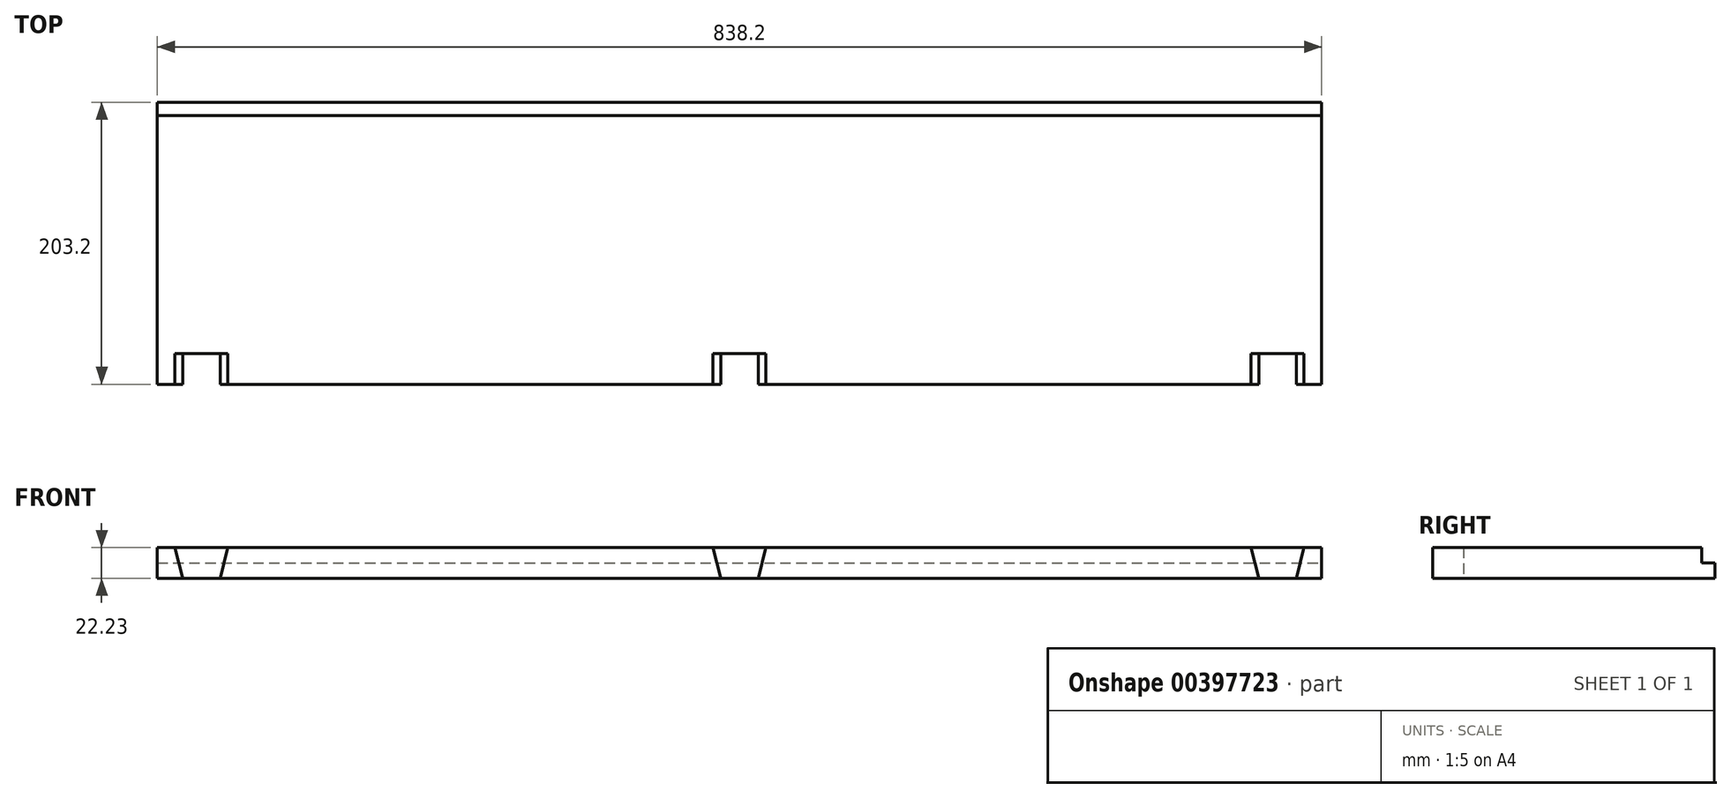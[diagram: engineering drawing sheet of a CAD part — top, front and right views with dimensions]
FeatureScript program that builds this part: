
annotation { "Feature Type Name" : "Feature", "Feature Type Description" : "" }
export const myFeature = defineFeature(function(context is Context, id is Id, definition is map)
    precondition{}
    {
        {
            var Q0;
            Q0=qCreatedBy(makeId("Top.planeOp"),FACE);
            var sketch = newSketch(context, id + "F0", { "sketchPlane" : qUnion([Q0])});
            skLineSegment(sketch, "E0.top", {"start": v(0, 0) * mm, "end": v(838.2, 0) * mm});
            skLineSegment(sketch, "E0.left", {"start": v(0, -203.2) * mm, "end": v(0, 0) * mm});
            skLineSegment(sketch, "E0.right", {"start": v(838.2, -203.2) * mm, "end": v(838.2, 0) * mm});
            skLineSegment(sketch, "E1.top", {"start": v(0, -203.2) * mm, "end": v(838.2, -203.2) * mm});
            skSolve(sketch);
        }
        {
            var Q0;
            Q0=makeQuery(id+"F0.imprint","IMPRINT",FACE,{"disambiguationData":[TD([[makeQuery(id+"F0.imprint","IMPRINT",EDGE,{"derivedFrom":sQuery(id+"F0.wireOp",EDGE,"E0.top")}),-1.0]])]});
            extrude(context, id + "F1", {"entities" : qUnion([Q0]), "depth" : 22.22 * mm});
        }
        {
            var Q0;
            Q0=makeQuery(id+"F1.opExtrude","CAP_FACE",FACE,{"disambiguationData":[OSD([sQuery(id+"F0.wireOp",EDGE,"E0.bottom"),sQuery(id+"F0.wireOp",EDGE,"E0.top"),sQuery(id+"F0.wireOp",EDGE,"E0.left"),sQuery(id+"F0.wireOp",EDGE,"E0.right"),sQuery(id+"F0.wireOp",EDGE,"E1.top"),sQuery(id+"F0.wireOp",EDGE,"E1.right"),sQuery(id+"F0.wireOp",EDGE,"6zvS0ofu-clFI-9DLG-dOLF-ekRLqX3uSt4N.top"),sQuery(id+"F0.wireOp",EDGE,"6zvS0ofu-clFI-9DLG-dOLF-ekRLqX3uSt4N.left")])],"isStart":false});
            var sketch = newSketch(context, id + "F2", { "sketchPlane" : qUnion([Q0])});
            skLineSegment(sketch, "E2.bottom", {"start": v(0, 0) * mm, "end": v(838.2, 0) * mm});
            skLineSegment(sketch, "E2.top", {"start": v(0, -9.52) * mm, "end": v(838.2, -9.52) * mm});
            skLineSegment(sketch, "E2.left", {"start": v(0, 0) * mm, "end": v(0, -9.52) * mm});
            skLineSegment(sketch, "E2.right", {"start": v(838.2, 0) * mm, "end": v(838.2, -9.52) * mm});
            skSolve(sketch);
        }
        {
            var Q0;
            Q0=makeQuery(id+"F2.imprint","IMPRINT",FACE,{"disambiguationData":[TD([[makeQuery(id+"F2.imprint","IMPRINT",EDGE,{"derivedFrom":sQuery(id+"F2.wireOp",EDGE,"E2.bottom")}),-1.0]])]});
            extrude(context, id + "F3", {"entities" : qUnion([Q0]), "operationType" : NewBodyOperationType.REMOVE, "oppositeDirection" : true, "depth" : 11.1 * mm});
        }
        {
            var Q0;
            Q0=makeQuery(id+"F1.opExtrude","SWEPT_FACE",FACE,{"disambiguationData":[OSD([sQuery(id+"F0.wireOp",EDGE,"E1.top")])]});
            var sketch = newSketch(context, id + "F4", { "sketchPlane" : qUnion([Q0])});
            skLineSegment(sketch, "E3", {"start": v(400.05, 22.23) * mm, "end": v(405.6, 0) * mm});
            skLineSegment(sketch, "E4", {"start": v(405.6, 0) * mm, "end": v(432.6, 0) * mm});
            skLineSegment(sketch, "E5", {"start": v(432.6, 0) * mm, "end": v(438.15, 22.23) * mm});
            skLineSegment(sketch, "E6", {"start": v(438.15, 22.23) * mm, "end": v(400.05, 22.23) * mm});
            skLineSegment(sketch, "E7.left", {"start": v(400.05, 22.23) * mm, "end": v(400.05, 0) * mm, "construction": true});
            skLineSegment(sketch, "E7.right", {"start": v(438.15, 22.23) * mm, "end": v(438.15, 0) * mm, "construction": true});
            skPoint(sketch, "E8", {"position": v(419.1, 22.23) * mm});
            skLineSegment(sketch, "E9", {"start": v(12.7, 22.23) * mm, "end": v(12.7, 0) * mm, "construction": true});
            skLineSegment(sketch, "E10", {"start": v(18.24, 0) * mm, "end": v(45.26, 0) * mm});
            skLineSegment(sketch, "E11", {"start": v(12.7, 22.23) * mm, "end": v(18.24, 0) * mm});
            skLineSegment(sketch, "E12", {"start": v(45.26, 0) * mm, "end": v(50.8, 22.23) * mm});
            skLineSegment(sketch, "E13", {"start": v(12.7, 0) * mm, "end": v(18.24, 0) * mm, "construction": true});
            skLineSegment(sketch, "E14.trimOffspring", {"start": v(50.8, 22.23) * mm, "end": v(12.7, 22.23) * mm});
            skLineSegment(sketch, "E15", {"start": v(825.5, 22.22) * mm, "end": v(787.4, 22.23) * mm});
            skLineSegment(sketch, "E16", {"start": v(787.4, 22.23) * mm, "end": v(787.4, 0) * mm, "construction": true});
            skLineSegment(sketch, "E17", {"start": v(787.4, 0) * mm, "end": v(792.94, 0) * mm, "construction": true});
            skLineSegment(sketch, "E18", {"start": v(792.94, 0) * mm, "end": v(787.4, 22.23) * mm});
            skLineSegment(sketch, "E19", {"start": v(825.5, 22.23) * mm, "end": v(825.5, 0) * mm, "construction": true});
            skLineSegment(sketch, "E20", {"start": v(825.5, 0) * mm, "end": v(819.96, 0) * mm, "construction": true});
            skLineSegment(sketch, "E21", {"start": v(825.5, 22.23) * mm, "end": v(819.96, 0) * mm});
            skLineSegment(sketch, "E22", {"start": v(792.94, 0) * mm, "end": v(819.96, 0) * mm});
            skSolve(sketch);
        }
        {
            var Q0;
            Q0=makeQuery(id+"F4.imprint","IMPRINT",FACE,{"disambiguationData":[TD([[makeQuery(id+"F4.imprint","IMPRINT",EDGE,{"derivedFrom":sQuery(id+"F4.wireOp",EDGE,"E3")}),1.0]])]});
            var Q1;
            Q1=makeQuery(id+"F4.imprint","IMPRINT",FACE,{"disambiguationData":[TD([[makeQuery(id+"F4.imprint","IMPRINT",EDGE,{"derivedFrom":sQuery(id+"F4.wireOp",EDGE,"E10")}),1.0]])]});
            var Q2;
            Q2=makeQuery(id+"F4.imprint","IMPRINT",FACE,{"disambiguationData":[TD([[makeQuery(id+"F4.imprint","IMPRINT",EDGE,{"derivedFrom":sQuery(id+"F4.wireOp",EDGE,"X6WF8ru8-tS9J-Vlz5-L0RJ-cluGKoGgCzeM")}),-1.0]])]});
            var Q3;
            Q3=makeQuery(id+"F4.imprint","IMPRINT",FACE,{"disambiguationData":[TD([[makeQuery(id+"F4.imprint","IMPRINT",EDGE,{"derivedFrom":sQuery(id+"F4.wireOp",EDGE,"E15")}),-1.0]])]});
            extrude(context, id + "F5", {"entities" : qUnion([Q0, Q1, Q2, Q3]), "operationType" : NewBodyOperationType.REMOVE, "oppositeDirection" : true, "depth" : 22.22 * mm});
        }
    });
